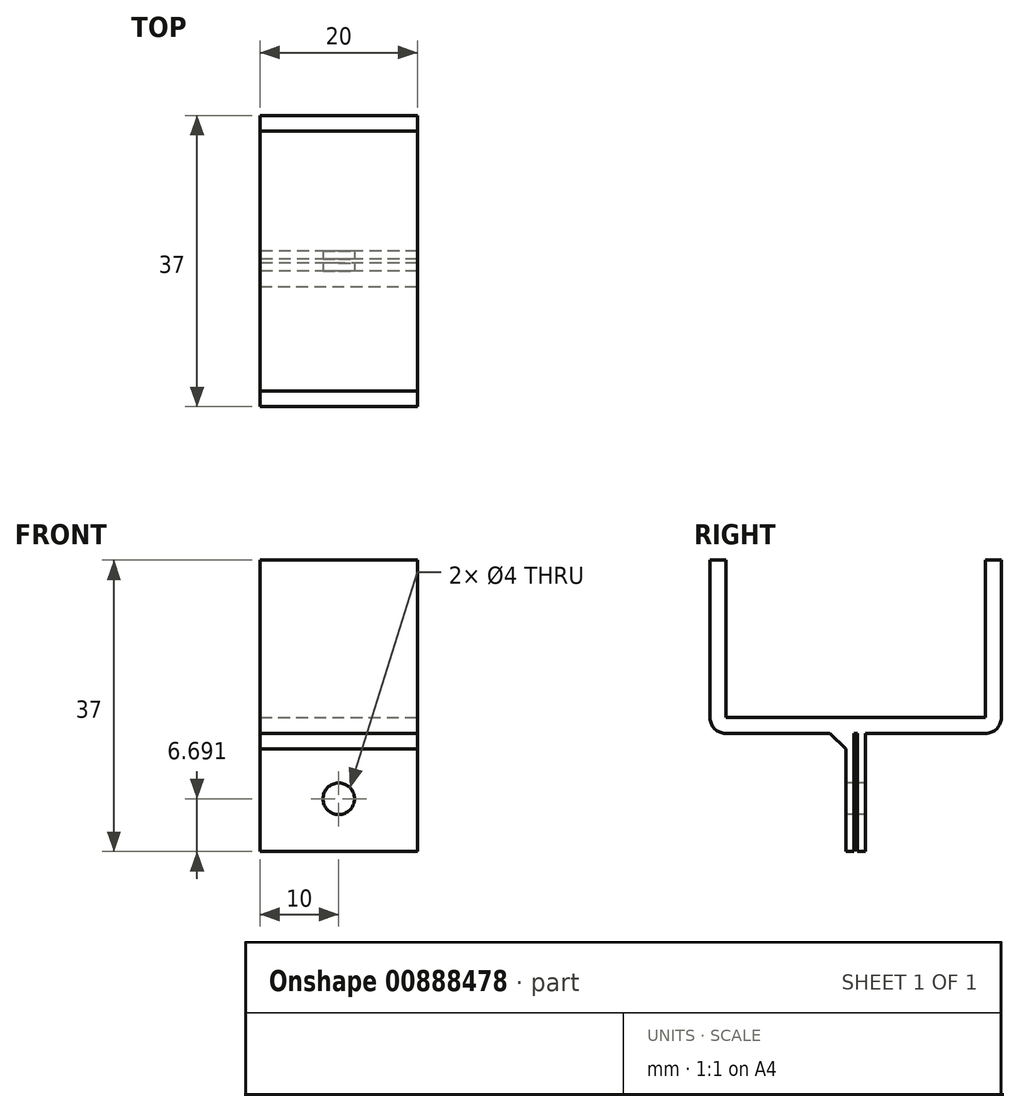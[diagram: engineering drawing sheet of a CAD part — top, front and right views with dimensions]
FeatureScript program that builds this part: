
annotation { "Feature Type Name" : "Feature", "Feature Type Description" : "" }
export const myFeature = defineFeature(function(context is Context, id is Id, definition is map)
    precondition{}
    {
        {
            var Q0;
            Q0=qCreatedBy(makeId("Top.planeOp"),FACE);
            var sketch = newSketch(context, id + "F0", { "sketchPlane" : qUnion([Q0])});
            skLineSegment(sketch, "E0.bottom", {"start": v(10, -18.5) * mm, "end": v(-10, -18.5) * mm});
            skLineSegment(sketch, "E0.top", {"start": v(10, 18.5) * mm, "end": v(-10, 18.5) * mm});
            skLineSegment(sketch, "E0.left", {"start": v(10, -18.5) * mm, "end": v(10, 18.5) * mm});
            skLineSegment(sketch, "E0.right", {"start": v(-10, -18.5) * mm, "end": v(-10, 18.5) * mm});
            skPoint(sketch, "E0.middle", {"position": v(0, 0) * mm});
            skSolve(sketch);
        }
        {
            var Q0;
            Q0=makeQuery(id+"F0.imprint","IMPRINT",FACE,{"disambiguationData":[TD([[makeQuery(id+"F0.imprint","IMPRINT",EDGE,{"derivedFrom":sQuery(id+"F0.wireOp",EDGE,"E0.bottom")}),-1.0]])]});
            extrude(context, id + "F1", {"entities" : qUnion([Q0]), "depth" : 2 * mm, "offsetDistance" : 25.4 * mm});
        }
        {
            var Q0;
            Q0=makeQuery(id+"F1.opExtrude","CAP_FACE",FACE,{"disambiguationData":[OSD([sQuery(id+"F0.wireOp",EDGE,"E0.bottom"),sQuery(id+"F0.wireOp",EDGE,"E0.top"),sQuery(id+"F0.wireOp",EDGE,"E0.left"),sQuery(id+"F0.wireOp",EDGE,"E0.right")])],"isStart":false});
            var sketch = newSketch(context, id + "F2", { "sketchPlane" : qUnion([Q0])});
            skLineSegment(sketch, "E1", {"start": v(-10, 16.5) * mm, "end": v(10, 16.5) * mm});
            skLineSegment(sketch, "E2", {"start": v(-10, -16.5) * mm, "end": v(10, -16.5) * mm});
            skSolve(sketch);
        }
        {
            var Q0;
            {var subQ0=sQuery(id+"F2.wireOp",EDGE,"E1");Q0=makeQuery(id+"F2.imprint","IMPRINT",FACE,{"disambiguationData":[TD([[makeQuery(id+"F2.imprint","IMPRINT",EDGE,{"derivedFrom":subQ0}),1.0]])]});}
            var Q1;
            {var subQ0=sQuery(id+"F2.wireOp",EDGE,"E2");Q1=makeQuery(id+"F2.imprint","IMPRINT",FACE,{"disambiguationData":[TD([[makeQuery(id+"F2.imprint","IMPRINT",EDGE,{"derivedFrom":subQ0}),-1.0]])]});}
            extrude(context, id + "F3", {"entities" : qUnion([Q0, Q1]), "operationType" : NewBodyOperationType.ADD, "depth" : 20 * mm, "offsetDistance" : 25 * mm});
        }
        {
            var Q0;
            Q0=makeQuery(id+"F1.opExtrude","CAP_FACE",FACE,{"disambiguationData":[OSD([sQuery(id+"F0.wireOp",EDGE,"E0.bottom"),sQuery(id+"F0.wireOp",EDGE,"E0.top"),sQuery(id+"F0.wireOp",EDGE,"E0.left"),sQuery(id+"F0.wireOp",EDGE,"E0.right")])],"isStart":true});
            var sketch = newSketch(context, id + "F4", { "sketchPlane" : qUnion([Q0])});
            skLineSegment(sketch, "E3.bottom", {"start": v(10, -1.25) * mm, "end": v(-10, -1.25) * mm});
            skLineSegment(sketch, "E3.top", {"start": v(10, -0.25) * mm, "end": v(-10, -0.25) * mm});
            skLineSegment(sketch, "E3.left", {"start": v(10, -1.25) * mm, "end": v(10, -0.25) * mm});
            skLineSegment(sketch, "E3.right", {"start": v(-10, -1.25) * mm, "end": v(-10, -0.25) * mm});
            skLineSegment(sketch, "E4.bottom", {"start": v(10, 0.25) * mm, "end": v(-10, 0.25) * mm});
            skLineSegment(sketch, "E4.top", {"start": v(10, 1.25) * mm, "end": v(-10, 1.25) * mm});
            skLineSegment(sketch, "E4.left", {"start": v(10, 0.25) * mm, "end": v(10, 1.25) * mm});
            skLineSegment(sketch, "E4.right", {"start": v(-10, 0.25) * mm, "end": v(-10, 1.25) * mm});
            skSolve(sketch);
        }
        {
            var Q0;
            Q0=makeQuery(id+"F4.imprint","IMPRINT",FACE,{"disambiguationData":[TD([[makeQuery(id+"F4.imprint","IMPRINT",EDGE,{"derivedFrom":sQuery(id+"F4.wireOp",EDGE,"E3.bottom")}),-1.0]])]});
            var Q1;
            Q1=makeQuery(id+"F4.imprint","IMPRINT",FACE,{"disambiguationData":[TD([[makeQuery(id+"F4.imprint","IMPRINT",EDGE,{"derivedFrom":sQuery(id+"F4.wireOp",EDGE,"E4.bottom")}),-1.0]])]});
            extrude(context, id + "F5", {"entities" : qUnion([Q0, Q1]), "operationType" : NewBodyOperationType.ADD, "depth" : 15 * mm, "offsetDistance" : 25 * mm});
        }
        {
            var Q0;
            Q0=makeQuery(id+"F5.opExtrude","CAP_EDGE",EDGE,{"disambiguationData":[OSD([sQuery(id+"F4.wireOp",EDGE,"E3.bottom")])],"isStart":true});
            var Q1;
            Q1=makeQuery(id+"F5.opExtrude","CAP_EDGE",EDGE,{"disambiguationData":[OSD([sQuery(id+"F4.wireOp",EDGE,"E4.top")])],"isStart":true});
            chamfer(context, id + "F6", {"entities" : qUnion([Q0, Q1]), "width" : 2 * mm, "tangentPropagation" : true});
        }
        {
            var Q0;
            Q0=makeQuery(id+"F1.opExtrude","CAP_EDGE",EDGE,{"disambiguationData":[OSD([sQuery(id+"F0.wireOp",EDGE,"E0.bottom")])],"isStart":true});
            var Q1;
            Q1=makeQuery(id+"F1.opExtrude","CAP_EDGE",EDGE,{"disambiguationData":[OSD([sQuery(id+"F0.wireOp",EDGE,"E0.top")])],"isStart":true});
            fillet(context, id + "F7", {"entities" : qUnion([Q0, Q1]), "radius" : 2 * mm, "tangentPropagation" : true, "allowEdgeOverflow" : false});
        }
        {
            var Q0;
            Q0=makeQuery(id+"F5.opExtrude","SWEPT_FACE",FACE,{"disambiguationData":[OSD([sQuery(id+"F4.wireOp",EDGE,"E4.top")])]});
            var sketch = newSketch(context, id + "F8", { "sketchPlane" : qUnion([Q0])});
            skPoint(sketch, "E5", {"position": v(0, -8.3) * mm});
            skSolve(sketch);
        }
        {
            var Q0;
            Q0=sQuery(id+"F8.wireOp",VERTEX,"E5");
            var Q1;
            Q1=makeQuery(id+"F1.opExtrude","SWEPT_BODY",BODY,{"disambiguationData":[OSD([sQuery(id+"F0.wireOp",EDGE,"E0.bottom"),sQuery(id+"F0.wireOp",EDGE,"E0.top"),sQuery(id+"F0.wireOp",EDGE,"E0.left"),sQuery(id+"F0.wireOp",EDGE,"E0.right")])]});
            hole(context, id + "F9", {"style" : HoleStyle.C_SINK, "endStyle" : HoleEndStyle.THROUGH, "holeDiameter" : 4 * mm, "cSinkDiameter" : 4 * mm, "cSinkAngle" : 90 * degree, "majorDiameter" : 5 * mm, "isTappedThrough" : true, "tappedDepth" : 12 * mm, "tapClearance" : 3, "locations" : qUnion([Q0]), "scope" : qUnion([Q1])});
        }
    });
